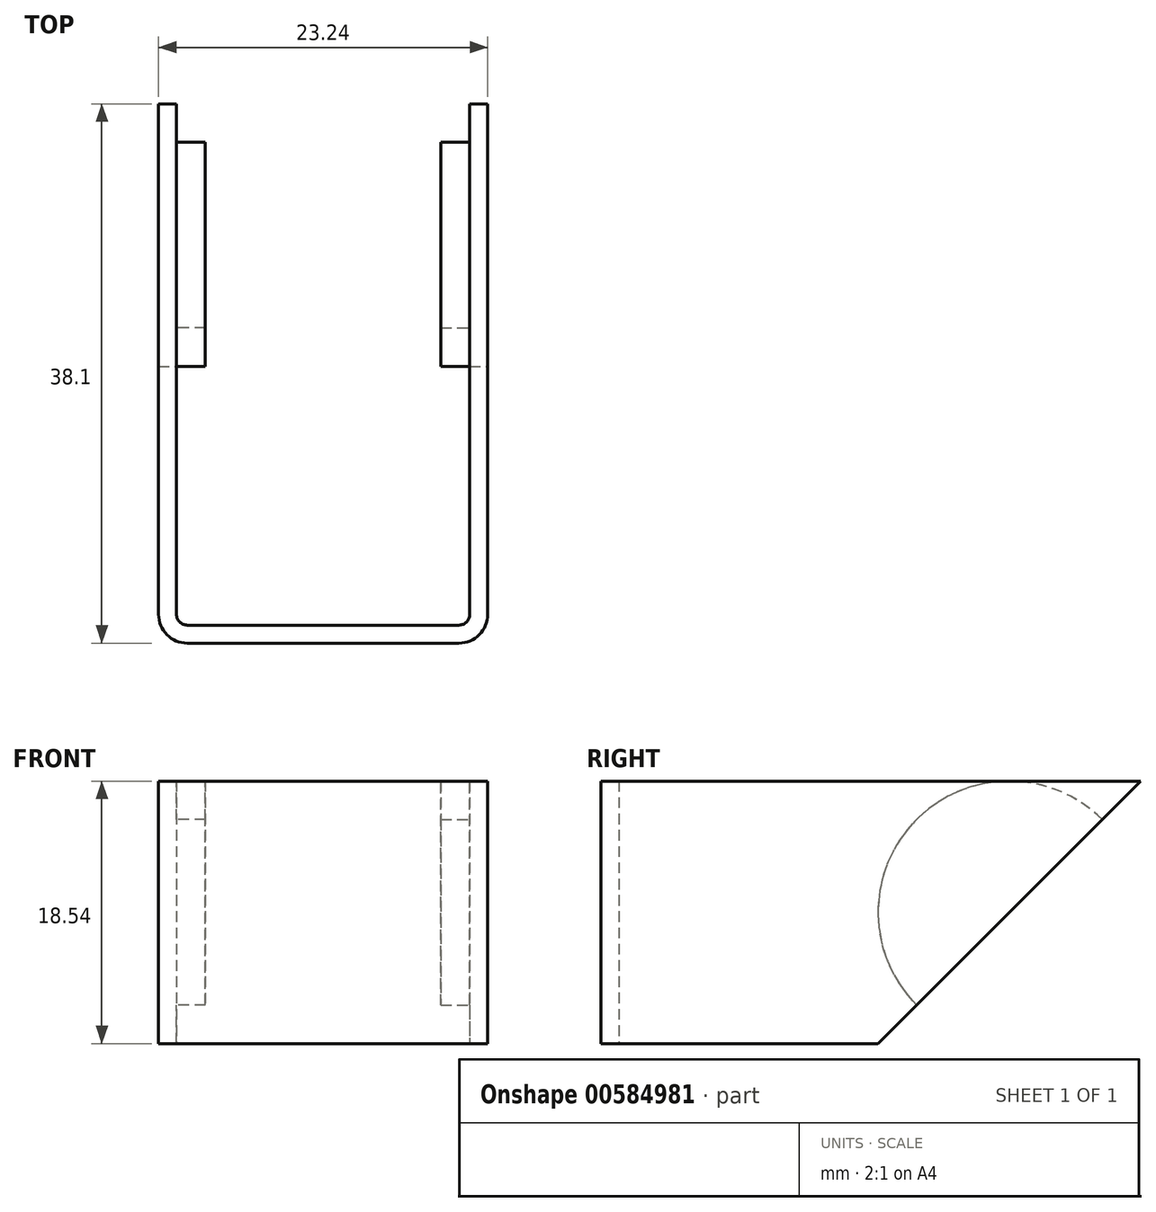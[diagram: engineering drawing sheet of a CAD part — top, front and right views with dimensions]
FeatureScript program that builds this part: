
annotation { "Feature Type Name" : "Feature", "Feature Type Description" : "" }
export const myFeature = defineFeature(function(context is Context, id is Id, definition is map)
    precondition{}
    {
        {
            var Q0;
            Q0=qCreatedBy(makeId("Top.planeOp"),FACE);
            var sketch = newSketch(context, id + "F0", { "sketchPlane" : qUnion([Q0])});
            skLineSegment(sketch, "E0", {"start": v(-11.62, 38.1) * mm, "end": v(-11.62, 2.03) * mm});
            skLineSegment(sketch, "E1", {"start": v(-9.59, 0) * mm, "end": v(9.59, 0) * mm});
            skLineSegment(sketch, "E2", {"start": v(11.62, 2.03) * mm, "end": v(11.62, 38.1) * mm});
            skLineSegment(sketch, "E3", {"start": v(11.62, 38.1) * mm, "end": v(10.35, 38.1) * mm});
            skLineSegment(sketch, "E4", {"start": v(10.35, 38.1) * mm, "end": v(10.35, 2.03) * mm});
            skLineSegment(sketch, "E5", {"start": v(9.59, 1.27) * mm, "end": v(-9.59, 1.27) * mm});
            skLineSegment(sketch, "E6", {"start": v(-10.35, 2.03) * mm, "end": v(-10.35, 38.1) * mm});
            skLineSegment(sketch, "E7", {"start": v(-10.35, 38.1) * mm, "end": v(-11.62, 38.1) * mm});
            skPoint(sketch, "E8.visualSharp", {"position": v(-10.35, 1.27) * mm});
            skArc(sketch, "E8.filletArc", {"start": v(-10.35, 2.03) * mm, "mid": v(-10.13, 1.5) * mm, "end": v(-9.59, 1.27) * mm});
            skPoint(sketch, "E9.visualSharp", {"position": v(10.35, 1.27) * mm});
            skArc(sketch, "E9.filletArc", {"start": v(9.59, 1.27) * mm, "mid": v(10.13, 1.5) * mm, "end": v(10.35, 2.03) * mm});
            skPoint(sketch, "E10.visualSharp", {"position": v(-11.62, 0) * mm});
            skArc(sketch, "E10.filletArc", {"start": v(-11.62, 2.03) * mm, "mid": v(-11.03, 0.6) * mm, "end": v(-9.59, 0) * mm});
            skPoint(sketch, "E11.visualSharp", {"position": v(11.62, 0) * mm});
            skArc(sketch, "E11.filletArc", {"start": v(9.59, 0) * mm, "mid": v(11.03, 0.6) * mm, "end": v(11.62, 2.03) * mm});
            skSolve(sketch);
        }
        {
            var Q0;
            Q0 = qSketchRegion(id + "F0", true);
            extrude(context, id + "F1", {"entities" : qUnion([Q0]), "depth" : 18.54 * mm, "offsetDistance" : 25.4 * mm});
        }
        {
            var Q0;
            Q0=makeQuery(id+"F1.opExtrude","SWEPT_FACE",FACE,{"disambiguationData":[OSD([sQuery(id+"F0.wireOp",EDGE,"E2")])]});
            var sketch = newSketch(context, id + "F2", { "sketchPlane" : qUnion([Q0])});
            skLineSegment(sketch, "E12", {"start": v(38.1, 18.54) * mm, "end": v(19.56, 0) * mm});
            skLineSegment(sketch, "E13", {"start": v(19.56, 0) * mm, "end": v(38.1, 0) * mm});
            skLineSegment(sketch, "E14", {"start": v(38.1, 0) * mm, "end": v(38.1, 18.54) * mm});
            skSolve(sketch);
        }
        {
            var Q0;
            Q0 = qSketchRegion(id + "F2", true);
            extrude(context, id + "F3", {"entities" : qUnion([Q0]), "operationType" : NewBodyOperationType.REMOVE, "endBound" : BoundingType.THROUGH_ALL, "oppositeDirection" : true, "depth" : 25.4 * mm, "offsetDistance" : 25.4 * mm});
        }
        {
            var Q0;
            Q0=makeQuery(id+"F1.opExtrude","SWEPT_FACE",FACE,{"disambiguationData":[OSD([sQuery(id+"F0.wireOp",EDGE,"E6")])]});
            var sketch = newSketch(context, id + "F4", { "sketchPlane" : qUnion([Q0])});
            skArc(sketch, "E15", {"start": v(35.38, 15.83) * mm, "mid": v(22.27, 15.83) * mm, "end": v(22.27, 2.72) * mm});
            skLineSegment(sketch, "E16", {"start": v(22.27, 2.72) * mm, "end": v(35.38, 15.83) * mm});
            skSolve(sketch);
        }
        {
            var Q0;
            Q0 = qSketchRegion(id + "F4", true);
            extrude(context, id + "F5", {"entities" : qUnion([Q0]), "operationType" : NewBodyOperationType.ADD, "depth" : 2.03 * mm, "offsetDistance" : 25.4 * mm});
        }
        {
            var Q0;
            Q0=makeQuery(id+"F1.opExtrude","SWEPT_FACE",FACE,{"disambiguationData":[OSD([sQuery(id+"F0.wireOp",EDGE,"E4")])]});
            var sketch = newSketch(context, id + "F6", { "sketchPlane" : qUnion([Q0])});
            skArc(sketch, "E17", {"start": v(-22.27, 2.72) * mm, "mid": v(-22.27, 15.83) * mm, "end": v(-35.38, 15.83) * mm});
            skLineSegment(sketch, "E18", {"start": v(-35.38, 15.83) * mm, "end": v(-22.27, 2.72) * mm});
            skSolve(sketch);
        }
        {
            var Q0;
            Q0 = qSketchRegion(id + "F6", true);
            extrude(context, id + "F7", {"entities" : qUnion([Q0]), "operationType" : NewBodyOperationType.ADD, "depth" : 2.03 * mm, "offsetDistance" : 25.4 * mm});
        }
    });
